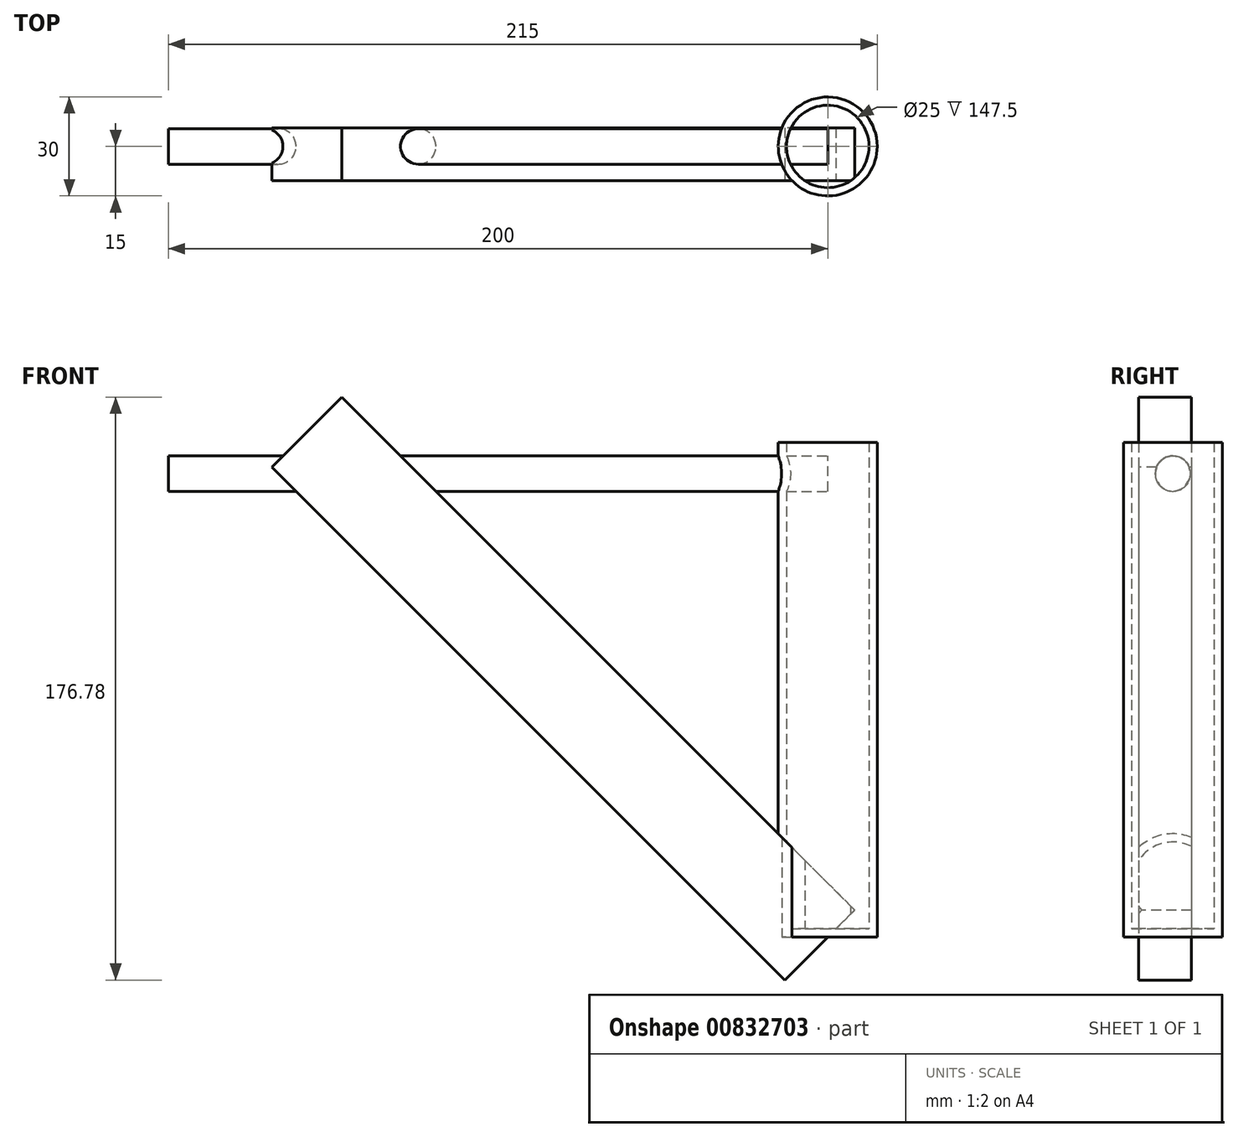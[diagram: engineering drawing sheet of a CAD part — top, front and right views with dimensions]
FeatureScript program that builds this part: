
annotation { "Feature Type Name" : "Feature", "Feature Type Description" : "" }
export const myFeature = defineFeature(function(context is Context, id is Id, definition is map)
    precondition{}
    {
        {
            var Q0;
            Q0=qCreatedBy(makeId("Top.planeOp"),FACE);
            var sketch = newSketch(context, id + "F0", { "sketchPlane" : qUnion([Q0])});
            skCircle(sketch, "E0", {"center": v(0, 0) * mm, "radius": 15 * mm});
            skSolve(sketch);
        }
        {
            var Q0;
            Q0=makeQuery(id+"F0.imprint","IMPRINT",FACE,{"disambiguationData":[TD([[makeQuery(id+"F0.imprint","IMPRINT",EDGE,{"derivedFrom":sQuery(id+"F0.wireOp",EDGE,"E0")}),1.0]])]});
            extrude(context, id + "F1", {"entities" : qUnion([Q0]), "depth" : 150 * mm, "offsetDistance" : 25 * mm});
        }
        {
            var Q0;
            Q0=makeQuery(id+"F1.opExtrude","CAP_FACE",FACE,{"disambiguationData":[OSD([sQuery(id+"F0.wireOp",EDGE,"E0")])],"isStart":false});
            shell(context, id + "F2", {"entities" : qUnion([Q0]), "thickness" : 2.5 * mm});
        }
        {
            var Q0;
            Q0=qCreatedBy(makeId("Right.planeOp"),FACE);
            var sketch = newSketch(context, id + "F3", { "sketchPlane" : qUnion([Q0])});
            skLineSegment(sketch, "E1", {"start": v(-43.92, 0) * mm, "end": v(41.14, 0) * mm});
            skSolve(sketch);
        }
        {
            var Q0;
            Q0=qCreatedBy(makeId("Right.planeOp"),FACE);
            var Q1;
            Q1=sQuery(id+"F3.wireOp",EDGE,"E1");
            cPlane(context, id + "F4", {"entities" : qUnion([Q0, Q1]), "cplaneType" : CPlaneType.LINE_ANGLE, "offset" : 0 * mm, "angle" : 45 * degree, "width" : 150 * mm, "height" : 150 * mm});
        }
        {
            var Q0;
            Q0=qCreatedBy(id+"F4.planeOp",FACE);
            var sketch = newSketch(context, id + "F5", { "sketchPlane" : qUnion([Q0])});
            skLineSegment(sketch, "E2.bottom", {"start": v(-5.61, 11.53) * mm, "end": v(10.39, 11.53) * mm});
            skLineSegment(sketch, "E2.top", {"start": v(-5.61, -18.47) * mm, "end": v(10.39, -18.47) * mm});
            skLineSegment(sketch, "E2.left", {"start": v(-5.61, 11.53) * mm, "end": v(-5.61, -18.47) * mm});
            skLineSegment(sketch, "E2.right", {"start": v(10.39, 11.53) * mm, "end": v(10.39, -18.47) * mm});
            skSolve(sketch);
        }
        {
            var Q0;
            Q0=makeQuery(id+"F5.imprint","IMPRINT",FACE,{"disambiguationData":[TD([[makeQuery(id+"F5.imprint","IMPRINT",EDGE,{"derivedFrom":sQuery(id+"F5.wireOp",EDGE,"E2.bottom")}),-1.0]])]});
            extrude(context, id + "F6", {"entities" : qUnion([Q0]), "operationType" : NewBodyOperationType.ADD, "depth" : 220 * mm, "offsetDistance" : 25 * mm});
        }
        {
            var Q0;
            Q0=qCreatedBy(makeId("Right.planeOp"),FACE);
            var sketch = newSketch(context, id + "F7", { "sketchPlane" : qUnion([Q0])});
            skCircle(sketch, "E3", {"center": v(0, 140.52) * mm, "radius": 5.38 * mm});
            skSolve(sketch);
        }
        {
            var Q0;
            Q0 = qSketchRegion(id + "F7", true);
            var Q1;
            {var subQ2=sQuery(id+"F5.wireOp",EDGE,"E2.bottom");Q1=makeQuery(id+"F6.boolean.opBoolean","SPLIT",FACE,{"disambiguationData":[TD([makeQuery(id+"F1.opExtrude","SWEPT_FACE",FACE,{"disambiguationData":[OSD([sQuery(id+"F0.wireOp",EDGE,"E0")])]})])],"derivedFrom":makeQuery(id+"F6.opExtrude","SWEPT_FACE",FACE,{"disambiguationData":[OSD([subQ2])]})});}
            extrude(context, id + "F8", {"entities" : qUnion([Q0]), "operationType" : NewBodyOperationType.ADD, "oppositeDirection" : true, "depth" : 200 * mm, "endBoundEntityFace" : qUnion([Q1]), "offsetDistance" : 25 * mm});
        }
    });
